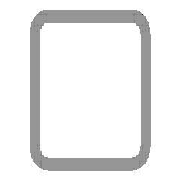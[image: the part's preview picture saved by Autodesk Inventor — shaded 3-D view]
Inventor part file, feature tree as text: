
AUTODESK INVENTOR PART (.ipt)
format: ipt  version: 2025.1 (Build 291241020, 241B)  size: 133,120 bytes
history: native  units: mm (DEFAULTED — no unit token found)
features: other x4, sketch x1, plane x1
ambient origin geometry x8: Origin, YZ Plane, XZ Plane, XY Plane, X Axis, Y Axis, Z Axis, Center Point
bodies: Solid1 (feature_tree), Body (feature_tree)
feature tree (6):
  parser-record x1  (decoder bookkeeping rows leaked as tree rows — omitted from the tree; the rows remain in map.json)
  other  "Driven Length"
  other  "Start Plane"
  other  "End Plane"
  sketch  "Sketch3"  dims[d3=600.0mm d4=0.0mm d7=4.0mm d9=40.0mm d11=40.0mm d12=2.0mm d13=-0.0mm d14=600.0mm d15=20.0mm d16=20.0mm d17=90.0deg d18=600.0mm]
  plane  "Work Plane3"
